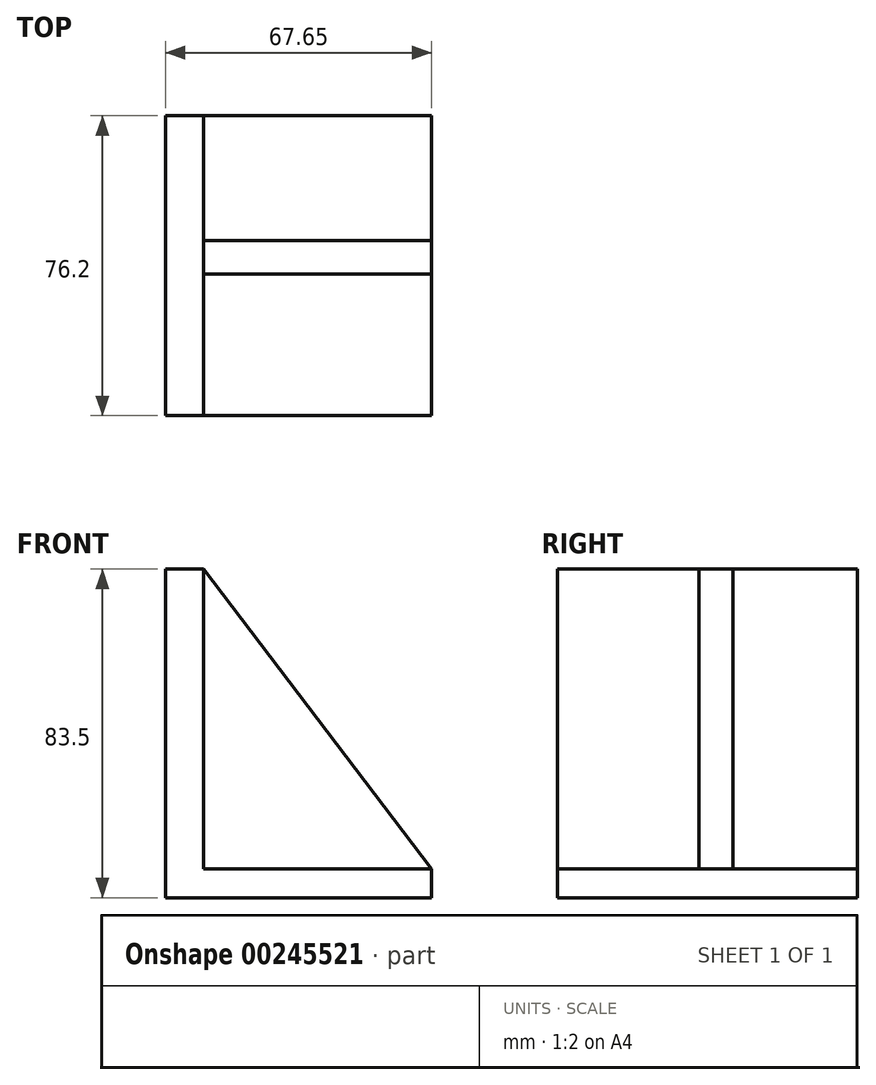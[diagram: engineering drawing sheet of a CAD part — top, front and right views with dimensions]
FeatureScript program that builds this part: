
annotation { "Feature Type Name" : "Feature", "Feature Type Description" : "" }
export const myFeature = defineFeature(function(context is Context, id is Id, definition is map)
    precondition{}
    {
        {
            var Q0;
            Q0=qCreatedBy(makeId("Front.planeOp"),FACE);
            var sketch = newSketch(context, id + "F0", { "sketchPlane" : qUnion([Q0])});
            skLineSegment(sketch, "E0.bottom", {"start": v(-46.19, 7.3) * mm, "end": v(21.46, 7.3) * mm});
            skLineSegment(sketch, "E0.top", {"start": v(-46.19, 0) * mm, "end": v(21.46, 0) * mm});
            skLineSegment(sketch, "E0.left", {"start": v(-46.19, 7.3) * mm, "end": v(-46.19, 0) * mm});
            skLineSegment(sketch, "E0.right", {"start": v(21.46, 7.3) * mm, "end": v(21.46, 0) * mm});
            skSolve(sketch);
        }
        {
            var Q0;
            Q0=makeQuery(id+"F0.imprint","IMPRINT",FACE,{"disambiguationData":[TD([[makeQuery(id+"F0.imprint","IMPRINT",EDGE,{"derivedFrom":sQuery(id+"F0.wireOp",EDGE,"E0.bottom")}),-1.0]])]});
            extrude(context, id + "F1", {"entities" : qUnion([Q0]), "oppositeDirection" : true, "depth" : 76.2 * mm});
        }
        {
            var Q0;
            Q0=makeQuery(id+"F1.opExtrude","SWEPT_FACE",FACE,{"disambiguationData":[OSD([sQuery(id+"F0.wireOp",EDGE,"E0.bottom")])]});
            var sketch = newSketch(context, id + "F2", { "sketchPlane" : qUnion([Q0])});
            skLineSegment(sketch, "E1", {"start": v(-36.5, 76.2) * mm, "end": v(-36.5, 0) * mm});
            skSolve(sketch);
        }
        {
            var Q0;
            Q0 = qSketchRegion(id + "F2", true);
            var Q1;
            {var subQ0=sQuery(id+"F2.wireOp",EDGE,"E1");Q1=makeQuery(id+"F2.imprint","IMPRINT",FACE,{"disambiguationData":[TD([[makeQuery(id+"F2.imprint","IMPRINT",EDGE,{"derivedFrom":subQ0}),-1.0]])]});}
            extrude(context, id + "F3", {"entities" : qUnion([Q0, Q1]), "operationType" : NewBodyOperationType.ADD, "depth" : 76.2 * mm});
        }
        {
            var Q0;
            Q0=makeQuery(id+"F1.opExtrude","SWEPT_FACE",FACE,{"disambiguationData":[OSD([sQuery(id+"F0.wireOp",EDGE,"E0.bottom")])]});
            var sketch = newSketch(context, id + "F4", { "sketchPlane" : qUnion([Q0])});
            skLineSegment(sketch, "E2.bottom", {"start": v(-36.5, 44.52) * mm, "end": v(21.46, 44.52) * mm});
            skLineSegment(sketch, "E2.top", {"start": v(-36.5, 35.96) * mm, "end": v(21.46, 35.96) * mm});
            skLineSegment(sketch, "E2.left", {"start": v(-36.5, 44.52) * mm, "end": v(-36.5, 35.96) * mm});
            skLineSegment(sketch, "E2.right", {"start": v(21.46, 44.52) * mm, "end": v(21.46, 35.96) * mm});
            skSolve(sketch);
        }
        {
            var Q0;
            Q0 = qSketchRegion(id + "F4", true);
            extrude(context, id + "F5", {"entities" : qUnion([Q0]), "operationType" : NewBodyOperationType.ADD, "depth" : 76.2 * mm});
        }
        {
            var Q0;
            Q0=makeQuery(id+"F5.opExtrude","SWEPT_FACE",FACE,{"disambiguationData":[OSD([sQuery(id+"F4.wireOp",EDGE,"E2.top")])]});
            var sketch = newSketch(context, id + "F6", { "sketchPlane" : qUnion([Q0])});
            skLineSegment(sketch, "E3", {"start": v(-36.5, 83.5) * mm, "end": v(21.46, 7.3) * mm});
            skSolve(sketch);
        }
        {
            var Q0;
            Q0=makeQuery(id+"F6.imprint","IMPRINT",FACE,{"disambiguationData":[TD([[makeQuery(id+"F6.imprint","IMPRINT",EDGE,{"derivedFrom":sQuery(id+"F6.wireOp",EDGE,"E3")}),1.0]])]});
            extrude(context, id + "F7", {"entities" : qUnion([Q0]), "operationType" : NewBodyOperationType.REMOVE, "endBound" : BoundingType.THROUGH_ALL, "oppositeDirection" : true, "depth" : 25.4 * mm});
        }
    });
